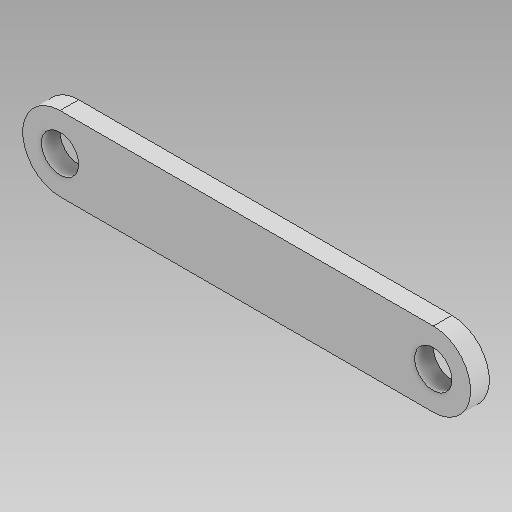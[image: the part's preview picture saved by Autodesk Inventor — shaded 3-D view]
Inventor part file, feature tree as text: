
AUTODESK INVENTOR PART (.ipt)
format: ipt  version: 2025 (Build 290162000, 162)  size: 94,720 bytes
history: native  units: in
note: dims shown in document units (in); Inventor stores cm internally (conversion verified against a paired STEP export)
features: other x1, extrude x1, sketch x1
ambient origin geometry x8: Origin, YZ Plane, XZ Plane, XY Plane, X Axis, Y Axis, Z Axis, Center Point
bodies: Body1 (feature_tree)
feature tree (3):
  other  "솔리드1"
  extrude  "돌출1"  Depth=0.7874in
  sketch  "스케치1"
